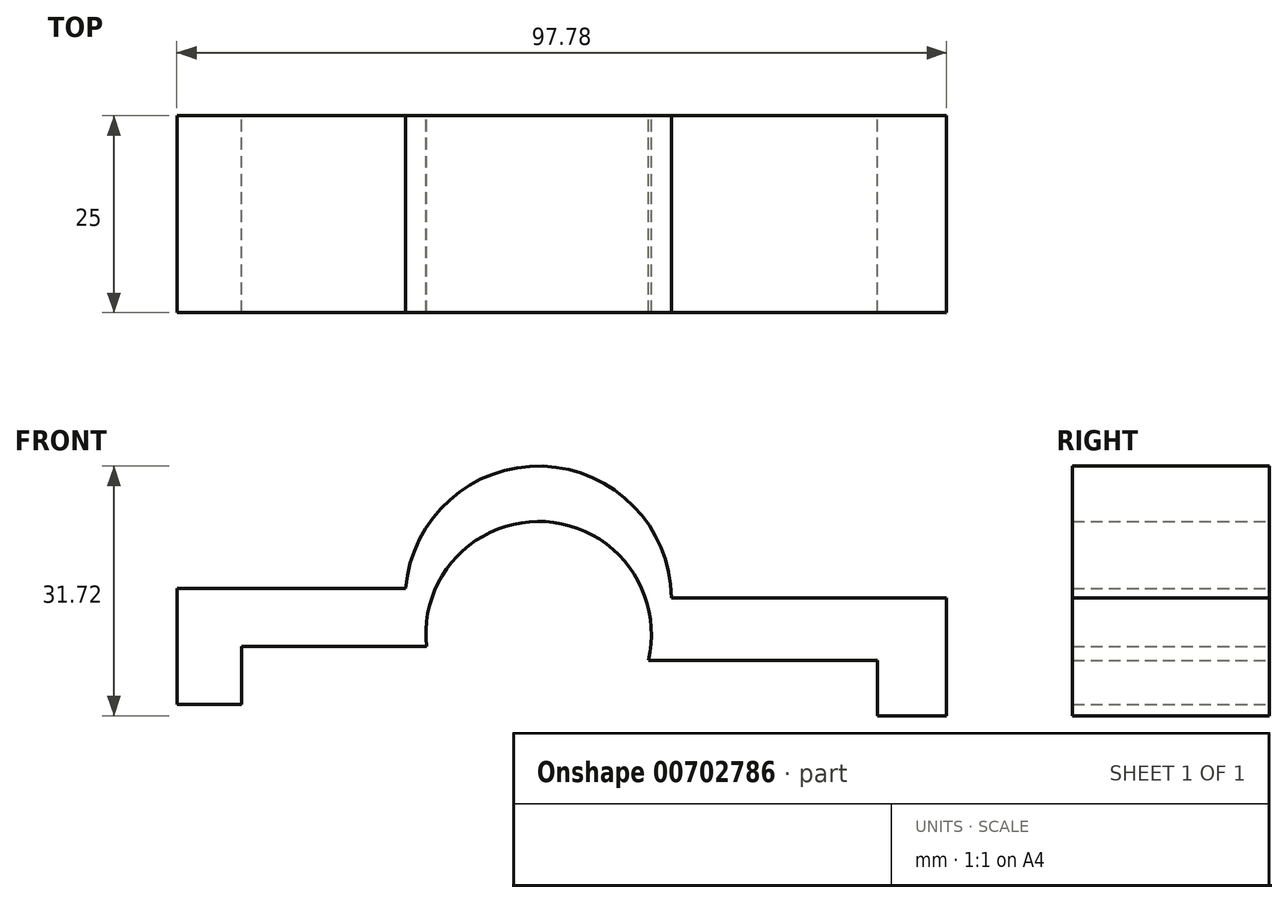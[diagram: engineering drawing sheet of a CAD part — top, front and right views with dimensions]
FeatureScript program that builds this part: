
annotation { "Feature Type Name" : "Feature", "Feature Type Description" : "" }
export const myFeature = defineFeature(function(context is Context, id is Id, definition is map)
    precondition{}
    {
        {
            var Q0;
            Q0=qCreatedBy(makeId("Front.planeOp"),FACE);
            var sketch = newSketch(context, id + "F0", { "sketchPlane" : qUnion([Q0])});
            skLineSegment(sketch, "E0", {"start": v(50.65, -44.63) * mm, "end": v(59.46, -44.63) * mm});
            skLineSegment(sketch, "E1", {"start": v(59.46, -44.63) * mm, "end": v(59.46, -29.66) * mm});
            skLineSegment(sketch, "E2", {"start": v(59.46, -29.66) * mm, "end": v(24.52, -29.66) * mm});
            skLineSegment(sketch, "E3", {"start": v(50.65, -44.63) * mm, "end": v(50.65, -37.58) * mm});
            skLineSegment(sketch, "E4", {"start": v(50.65, -37.58) * mm, "end": v(21.58, -37.58) * mm});
            skLineSegment(sketch, "E5", {"start": v(-38.32, -28.48) * mm, "end": v(-38.32, -43.16) * mm});
            skLineSegment(sketch, "E6", {"start": v(-38.32, -43.16) * mm, "end": v(-30.1, -43.16) * mm});
            skLineSegment(sketch, "E7", {"start": v(-30.1, -43.16) * mm, "end": v(-30.1, -35.82) * mm});
            skLineSegment(sketch, "E8", {"start": v(-30.1, -35.82) * mm, "end": v(-6.6, -35.82) * mm});
            skLineSegment(sketch, "E9", {"start": v(-38.32, -28.48) * mm, "end": v(-9.25, -28.48) * mm});
            skArc(sketch, "E10", {"start": v(21.58, -37.58) * mm, "mid": v(8.53, -19.98) * mm, "end": v(-6.6, -35.82) * mm});
            skArc(sketch, "E11", {"start": v(24.52, -29.66) * mm, "mid": v(8.2, -12.92) * mm, "end": v(-9.25, -28.48) * mm});
            skSolve(sketch);
        }
        {
            var Q0;
            Q0 = qSketchRegion(id + "F0", true);
            extrude(context, id + "F1", {"entities" : qUnion([Q0]), "depth" : 25 * mm, "offsetDistance" : 25 * mm});
        }
    });
